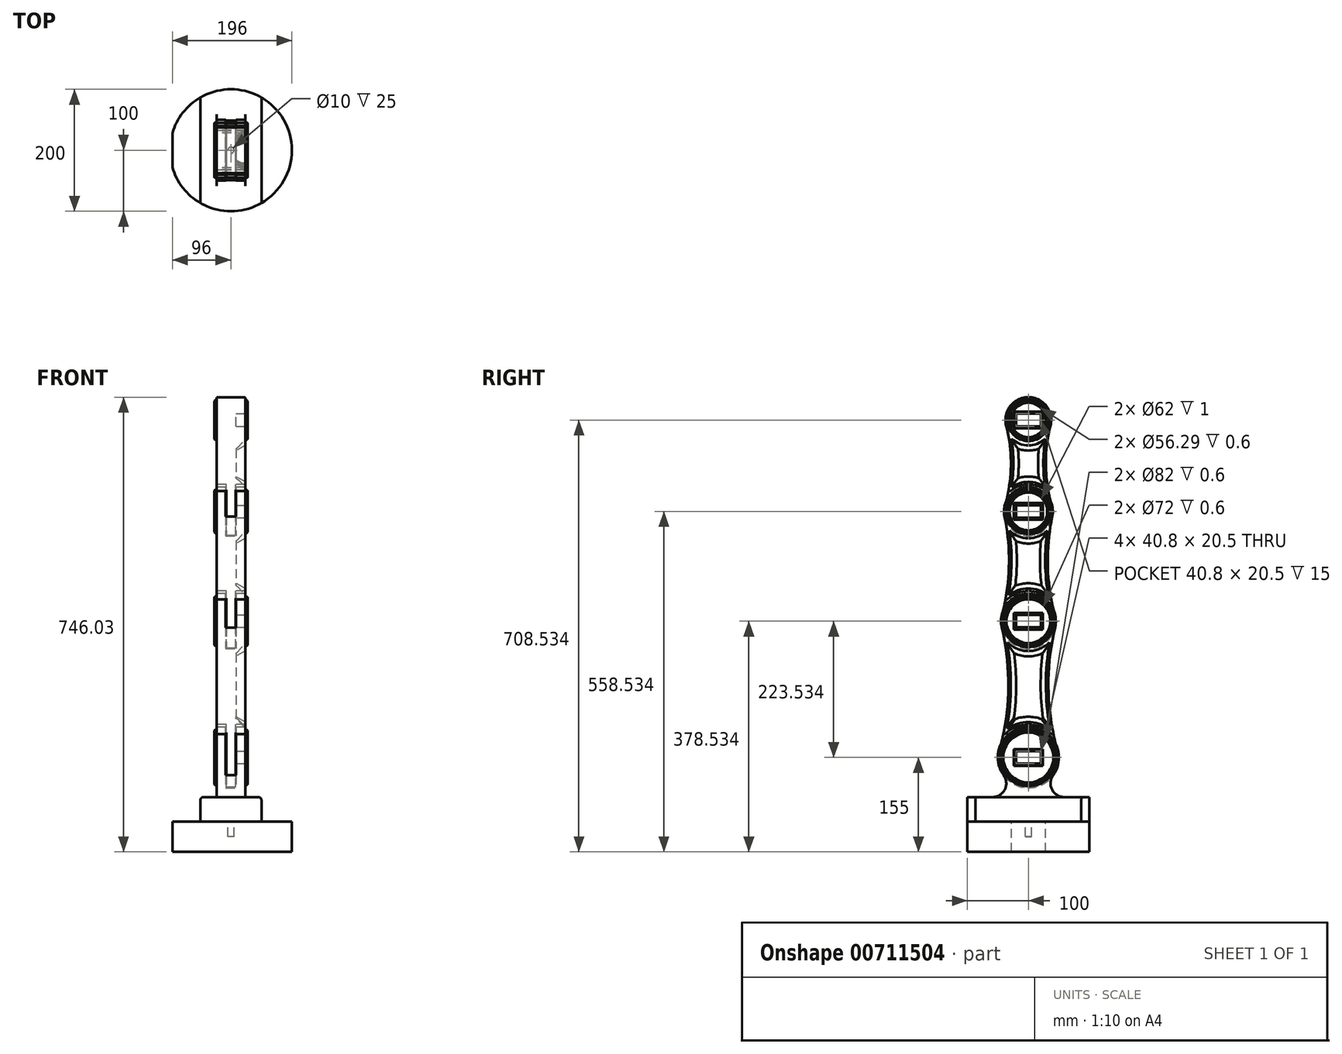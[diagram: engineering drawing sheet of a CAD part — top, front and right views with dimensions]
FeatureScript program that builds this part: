
annotation { "Feature Type Name" : "Feature", "Feature Type Description" : "" }
export const myFeature = defineFeature(function(context is Context, id is Id, definition is map)
    precondition{}
    {
        {
            var Q0;
            Q0=qCreatedBy(makeId("Top.planeOp"),FACE);
            var sketch = newSketch(context, id + "F0", { "sketchPlane" : qUnion([Q0])});
            skArc(sketch, "E0", {"start": v(-96, -28) * mm, "mid": v(100, 0) * mm, "end": v(-96, 28) * mm});
            skLineSegment(sketch, "E1", {"start": v(-50, 86.6) * mm, "end": v(-50, -86.6) * mm});
            skLineSegment(sketch, "E2", {"start": v(50, 86.6) * mm, "end": v(50, -86.6) * mm});
            skLineSegment(sketch, "E3", {"start": v(-96, 28) * mm, "end": v(-96, -28) * mm});
            skSolve(sketch);
        }
        {
            var Q0;
            Q0 = qSketchRegion(id + "F0", true);
            extrude(context, id + "F1", {"entities" : qUnion([Q0]), "oppositeDirection" : true, "depth" : 50 * mm, "offsetDistance" : 25 * mm});
        }
        {
            var Q0;
            {var subQ0=sQuery(id+"F0.wireOp",EDGE,"E1");Q0=makeQuery(id+"F0.imprint","IMPRINT",FACE,{"disambiguationData":[TD([[makeQuery(id+"F0.imprint","IMPRINT",EDGE,{"derivedFrom":subQ0}),1.0]])]});}
            extrude(context, id + "F2", {"entities" : qUnion([Q0]), "depth" : 40 * mm, "offsetDistance" : 25 * mm});
        }
        {
            var Q0;
            Q0=qCreatedBy(makeId("Right.planeOp"),FACE);
            var sketch = newSketch(context, id + "F3", { "sketchPlane" : qUnion([Q0])});
            skCircle(sketch, "E4", {"center": v(0, 105) * mm, "radius": 50 * mm});
            skArc(sketch, "E5", {"start": v(-58.74, 40) * mm, "mid": v(-38.7, 52.27) * mm, "end": v(-40.5, 75.69) * mm});
            skArc(sketch, "E6", {"start": v(40.5, 75.69) * mm, "mid": v(38.7, 52.27) * mm, "end": v(58.74, 40) * mm});
            skLineSegment(sketch, "E7", {"start": v(-58.74, 40) * mm, "end": v(58.74, 40) * mm});
            skSolve(sketch);
        }
        {
            var Q0;
            Q0 = qSketchRegion(id + "F3", true);
            extrude(context, id + "F4", {"entities" : qUnion([Q0]), "operationType" : NewBodyOperationType.ADD, "endBound" : BoundingType.SYMMETRIC, "depth" : 47 * mm, "offsetDistance" : 25 * mm});
        }
        {
            var Q0;
            {var subQ0=sQuery(id+"F3.wireOp",EDGE,"E4");var subQ1=makeQuery(id+"F3.imprint","INTERSECT",VERTEX,{"derivedFrom":[subQ0,sQuery(id+"F3.wireOp",EDGE,"E5")]});Q0=makeQuery(id+"F3.imprint","IMPRINT",FACE,{"disambiguationData":[TD([[makeQuery(id+"F3.imprint","IMPRINT",EDGE,{"disambiguationData":[TD([[subQ1,-1.0]])],"derivedFrom":subQ0}),1.0]])]});}
            extrude(context, id + "F5", {"entities" : qUnion([Q0]), "operationType" : NewBodyOperationType.REMOVE, "endBound" : BoundingType.SYMMETRIC, "oppositeDirection" : true, "depth" : 17 * mm, "offsetDistance" : 25 * mm});
        }
        {
            var Q0;
            Q0=qCreatedBy(makeId("Right.planeOp"),FACE);
            var sketch = newSketch(context, id + "F6", { "sketchPlane" : qUnion([Q0])});
            skCircle(sketch, "E8.0", {"center": v(0, 105) * mm, "radius": 49 * mm});
            skCircle(sketch, "E9", {"center": v(0, 328.53) * mm, "radius": 45 * mm});
            skArc(sketch, "E10", {"start": v(-47.22, 118.07) * mm, "mid": v(-32.8, 217.84) * mm, "end": v(-43.76, 318.04) * mm});
            skArc(sketch, "E11", {"start": v(43.76, 318.04) * mm, "mid": v(32.8, 217.84) * mm, "end": v(47.22, 118.07) * mm});
            skArc(sketch, "E12.0", {"start": v(42.07, 138.86) * mm, "mid": v(0, 159) * mm, "end": v(-42.07, 138.86) * mm});
            skArc(sketch, "E13.0", {"start": v(-34.7, 293.93) * mm, "mid": v(0, 279.53) * mm, "end": v(34.7, 293.93) * mm});
            skArc(sketch, "E14.0", {"start": v(34.7, 293.93) * mm, "mid": v(28.74, 222.34) * mm, "end": v(35.56, 150.82) * mm});
            skArc(sketch, "E15.0", {"start": v(-35.56, 150.82) * mm, "mid": v(-28.74, 222.34) * mm, "end": v(-34.7, 293.93) * mm});
            skArc(sketch, "E16.0", {"start": v(35.56, 150.82) * mm, "mid": v(0, 163) * mm, "end": v(-35.56, 150.82) * mm});
            skSolve(sketch);
        }
        {
            var Q0;
            Q0 = qSketchRegion(id + "F6", true);
            extrude(context, id + "F7", {"entities" : qUnion([Q0]), "endBound" : BoundingType.SYMMETRIC, "depth" : 15 * mm, "offsetDistance" : 25 * mm});
        }
        {
            var Q0;
            {var subQ5=sQuery(id+"F6.wireOp",EDGE,"E12.0");Q0=makeQuery(id+"F6.imprint","IMPRINT",FACE,{"disambiguationData":[TD([[makeQuery(id+"F6.imprint","IMPRINT",EDGE,{"derivedFrom":subQ5}),-1.0]])]});}
            var Q1;
            {var subQ0=sQuery(id+"F6.wireOp",EDGE,"E9");var subQ1=makeQuery(id+"F6.imprint","INTERSECT",VERTEX,{"derivedFrom":[subQ0,sQuery(id+"F6.wireOp",EDGE,"E10")]});Q1=makeQuery(id+"F6.imprint","IMPRINT",FACE,{"disambiguationData":[TD([[makeQuery(id+"F6.imprint","IMPRINT",EDGE,{"disambiguationData":[TD([[subQ1,-1.0]])],"derivedFrom":subQ0}),1.0]])]});}
            var Q2;
            Q2=makeQuery(id+"F6.imprint","IMPRINT",FACE,{"disambiguationData":[TD([[makeQuery(id+"F6.imprint","IMPRINT",EDGE,{"derivedFrom":sQuery(id+"F6.wireOp",EDGE,"E13.0")}),-1.0]])]});
            extrude(context, id + "F8", {"entities" : qUnion([Q0, Q1, Q2]), "operationType" : NewBodyOperationType.ADD, "endBound" : BoundingType.SYMMETRIC, "depth" : 47 * mm, "offsetDistance" : 25 * mm});
        }
        {
            var Q0;
            Q0=makeQuery(id+"F8.opExtrude","CAP_FACE",FACE,{"disambiguationData":[OSD([sQuery(id+"F6.wireOp",EDGE,"E9"),sQuery(id+"F6.wireOp",EDGE,"E10"),sQuery(id+"F6.wireOp",EDGE,"E11"),sQuery(id+"F6.wireOp",EDGE,"E12.0")])],"isStart":false});
            var sketch = newSketch(context, id + "F9", { "sketchPlane" : qUnion([Q0])});
            skArc(sketch, "E17.0", {"start": v(-35.56, 150.82) * mm, "mid": v(0, 163) * mm, "end": v(35.56, 150.82) * mm});
            skArc(sketch, "E17.1", {"start": v(-34.7, 293.93) * mm, "mid": v(-28.74, 222.34) * mm, "end": v(-35.56, 150.82) * mm});
            skArc(sketch, "E17.2", {"start": v(34.7, 293.93) * mm, "mid": v(0, 279.53) * mm, "end": v(-34.7, 293.93) * mm});
            skArc(sketch, "E17.3", {"start": v(35.56, 150.82) * mm, "mid": v(28.74, 222.34) * mm, "end": v(34.7, 293.93) * mm});
            skSolve(sketch);
        }
        {
            var Q0;
            Q0 = qSketchRegion(id + "F9", true);
            extrude(context, id + "F10", {"entities" : qUnion([Q0]), "operationType" : NewBodyOperationType.REMOVE, "oppositeDirection" : true, "depth" : 15 * mm, "offsetDistance" : 25 * mm, "hasDraft" : true, "draftAngle" : 30 * degree, "draftPullDirection" : true});
        }
        {
            var Q0;
            {var subQ0=sQuery(id+"F6.wireOp",EDGE,"E9");var subQ1=makeQuery(id+"F6.imprint","INTERSECT",VERTEX,{"derivedFrom":[subQ0,sQuery(id+"F6.wireOp",EDGE,"E10")]});Q0=makeQuery(id+"F6.imprint","IMPRINT",FACE,{"disambiguationData":[TD([[makeQuery(id+"F6.imprint","IMPRINT",EDGE,{"disambiguationData":[TD([[subQ1,-1.0]])],"derivedFrom":subQ0}),1.0]])]});}
            extrude(context, id + "F11", {"entities" : qUnion([Q0]), "operationType" : NewBodyOperationType.REMOVE, "endBound" : BoundingType.SYMMETRIC, "oppositeDirection" : true, "depth" : 17 * mm, "offsetDistance" : 25 * mm});
        }
        {
            var Q0;
            Q0=qCreatedBy(makeId("Right.planeOp"),FACE);
            var sketch = newSketch(context, id + "F12", { "sketchPlane" : qUnion([Q0])});
            skCircle(sketch, "E18", {"center": v(0, 328.53) * mm, "radius": 44.5 * mm});
            skCircle(sketch, "E19", {"center": v(0, 508.53) * mm, "radius": 40 * mm});
            skArc(sketch, "E20", {"start": v(-43.05, 339.8) * mm, "mid": v(-31.77, 419.82) * mm, "end": v(-39.15, 500.3) * mm});
            skArc(sketch, "E21", {"start": v(39.15, 500.3) * mm, "mid": v(31.77, 419.82) * mm, "end": v(43.05, 339.8) * mm});
            skArc(sketch, "E22.0", {"start": v(38.46, 359.69) * mm, "mid": v(0, 378.03) * mm, "end": v(-38.46, 359.69) * mm});
            skSolve(sketch);
        }
        {
            var Q0;
            Q0 = qSketchRegion(id + "F12", true);
            extrude(context, id + "F13", {"entities" : qUnion([Q0]), "endBound" : BoundingType.SYMMETRIC, "depth" : 15 * mm, "offsetDistance" : 25 * mm});
        }
        {
            var Q0;
            {var subQ0=sQuery(id+"F12.wireOp",EDGE,"E19");var subQ1=makeQuery(id+"F12.imprint","INTERSECT",VERTEX,{"derivedFrom":[subQ0,sQuery(id+"F12.wireOp",EDGE,"E20")]});Q0=makeQuery(id+"F12.imprint","IMPRINT",FACE,{"disambiguationData":[TD([[makeQuery(id+"F12.imprint","IMPRINT",EDGE,{"disambiguationData":[TD([[subQ1,-1.0]])],"derivedFrom":subQ0}),1.0]])]});}
            var Q1;
            {var subQ5=sQuery(id+"F12.wireOp",EDGE,"E22.0");Q1=makeQuery(id+"F12.imprint","IMPRINT",FACE,{"disambiguationData":[TD([[makeQuery(id+"F12.imprint","IMPRINT",EDGE,{"derivedFrom":subQ5}),-1.0]])]});}
            extrude(context, id + "F14", {"entities" : qUnion([Q0, Q1]), "operationType" : NewBodyOperationType.ADD, "endBound" : BoundingType.SYMMETRIC, "depth" : 47 * mm, "offsetDistance" : 25 * mm});
        }
        {
            var Q0;
            Q0=makeQuery(id+"F14.opExtrude","CAP_FACE",FACE,{"disambiguationData":[OSD([sQuery(id+"F12.wireOp",EDGE,"E19"),sQuery(id+"F12.wireOp",EDGE,"E20"),sQuery(id+"F12.wireOp",EDGE,"E21"),sQuery(id+"F12.wireOp",EDGE,"E22.0")])],"isStart":false});
            var sketch = newSketch(context, id + "F15", { "sketchPlane" : qUnion([Q0])});
            skArc(sketch, "E23.0", {"start": v(-32.31, 371.17) * mm, "mid": v(0, 382.03) * mm, "end": v(32.31, 371.17) * mm});
            skArc(sketch, "E23.1", {"start": v(-31.08, 477.39) * mm, "mid": v(-27.69, 424.23) * mm, "end": v(-32.31, 371.17) * mm});
            skArc(sketch, "E23.2", {"start": v(31.08, 477.39) * mm, "mid": v(0, 464.53) * mm, "end": v(-31.08, 477.39) * mm});
            skArc(sketch, "E23.3", {"start": v(32.31, 371.17) * mm, "mid": v(27.69, 424.23) * mm, "end": v(31.08, 477.39) * mm});
            skSolve(sketch);
        }
        {
            var Q0;
            Q0 = qSketchRegion(id + "F15", true);
            extrude(context, id + "F16", {"entities" : qUnion([Q0]), "operationType" : NewBodyOperationType.REMOVE, "oppositeDirection" : true, "depth" : 15 * mm, "offsetDistance" : 25 * mm, "hasDraft" : true, "draftAngle" : 30 * degree, "draftPullDirection" : true});
        }
        {
            var Q0;
            {var subQ0=sQuery(id+"F12.wireOp",EDGE,"E19");var subQ1=makeQuery(id+"F12.imprint","INTERSECT",VERTEX,{"derivedFrom":[subQ0,sQuery(id+"F12.wireOp",EDGE,"E20")]});Q0=makeQuery(id+"F12.imprint","IMPRINT",FACE,{"disambiguationData":[TD([[makeQuery(id+"F12.imprint","IMPRINT",EDGE,{"disambiguationData":[TD([[subQ1,-1.0]])],"derivedFrom":subQ0}),1.0]])]});}
            extrude(context, id + "F17", {"entities" : qUnion([Q0]), "operationType" : NewBodyOperationType.REMOVE, "endBound" : BoundingType.SYMMETRIC, "oppositeDirection" : true, "depth" : 17 * mm, "offsetDistance" : 25 * mm});
        }
        {
            var Q0;
            Q0=qCreatedBy(makeId("Right.planeOp"),FACE);
            var sketch = newSketch(context, id + "F18", { "sketchPlane" : qUnion([Q0])});
            skCircle(sketch, "E24", {"center": v(0, 508.53) * mm, "radius": 39.5 * mm});
            skCircle(sketch, "E25", {"center": v(0, 658.53) * mm, "radius": 37.5 * mm});
            skArc(sketch, "E26", {"start": v(-38, 519.3) * mm, "mid": v(-28.58, 584.16) * mm, "end": v(-36.33, 649.25) * mm});
            skArc(sketch, "E27", {"start": v(36.33, 649.25) * mm, "mid": v(28.58, 584.16) * mm, "end": v(38, 519.3) * mm});
            skArc(sketch, "E28.0", {"start": v(33.52, 537.8) * mm, "mid": v(0, 553.03) * mm, "end": v(-33.52, 537.8) * mm});
            skSolve(sketch);
        }
        {
            var Q0;
            Q0 = qSketchRegion(id + "F18", true);
            extrude(context, id + "F19", {"entities" : qUnion([Q0]), "endBound" : BoundingType.SYMMETRIC, "depth" : 15 * mm, "offsetDistance" : 25 * mm});
        }
        {
            var Q0;
            {var subQ5=sQuery(id+"F18.wireOp",EDGE,"E28.0");Q0=makeQuery(id+"F18.imprint","IMPRINT",FACE,{"disambiguationData":[TD([[makeQuery(id+"F18.imprint","IMPRINT",EDGE,{"derivedFrom":subQ5}),-1.0]])]});}
            var Q1;
            {var subQ0=sQuery(id+"F18.wireOp",EDGE,"E25");var subQ1=makeQuery(id+"F18.imprint","INTERSECT",VERTEX,{"derivedFrom":[subQ0,sQuery(id+"F18.wireOp",EDGE,"E26")]});Q1=makeQuery(id+"F18.imprint","IMPRINT",FACE,{"disambiguationData":[TD([[makeQuery(id+"F18.imprint","IMPRINT",EDGE,{"disambiguationData":[TD([[subQ1,-1.0]])],"derivedFrom":subQ0}),1.0]])]});}
            extrude(context, id + "F20", {"entities" : qUnion([Q0, Q1]), "operationType" : NewBodyOperationType.ADD, "endBound" : BoundingType.SYMMETRIC, "depth" : 47 * mm, "offsetDistance" : 25 * mm});
        }
        {
            var Q0;
            Q0=makeQuery(id+"F20.opExtrude","CAP_FACE",FACE,{"disambiguationData":[OSD([sQuery(id+"F18.wireOp",EDGE,"E25"),sQuery(id+"F18.wireOp",EDGE,"E26"),sQuery(id+"F18.wireOp",EDGE,"E27"),sQuery(id+"F18.wireOp",EDGE,"E28.0")])],"isStart":false});
            var sketch = newSketch(context, id + "F21", { "sketchPlane" : qUnion([Q0])});
            skArc(sketch, "E29.0", {"start": v(-27.56, 548.44) * mm, "mid": v(0, 557.03) * mm, "end": v(27.56, 548.44) * mm});
            skArc(sketch, "E29.1", {"start": v(-27.78, 627.7) * mm, "mid": v(-24.56, 588.08) * mm, "end": v(-27.56, 548.44) * mm});
            skArc(sketch, "E29.2", {"start": v(27.78, 627.7) * mm, "mid": v(0, 617.03) * mm, "end": v(-27.78, 627.7) * mm});
            skArc(sketch, "E29.3", {"start": v(27.56, 548.44) * mm, "mid": v(24.56, 588.08) * mm, "end": v(27.78, 627.7) * mm});
            skSolve(sketch);
        }
        {
            var Q0;
            Q0 = qSketchRegion(id + "F21", true);
            extrude(context, id + "F22", {"entities" : qUnion([Q0]), "operationType" : NewBodyOperationType.REMOVE, "oppositeDirection" : true, "depth" : 15 * mm, "offsetDistance" : 25 * mm, "hasDraft" : true, "draftAngle" : 30 * degree, "draftPullDirection" : true});
        }
        {
            var Q0;
            Q0=qCreatedBy(makeId("Front.planeOp"),FACE);
            var sketch = newSketch(context, id + "F23", { "sketchPlane" : qUnion([Q0])});
            skLineSegment(sketch, "E30", {"start": v(27.5, 149) * mm, "end": v(27.5, 146) * mm});
            skLineSegment(sketch, "E31", {"start": v(27.5, 149) * mm, "end": v(23.5, 152.36) * mm});
            skLineSegment(sketch, "E32", {"start": v(23.5, 152.36) * mm, "end": v(23.5, 105) * mm});
            skLineSegment(sketch, "E33", {"start": v(23.5, 105) * mm, "end": v(26.9, 105) * mm});
            skLineSegment(sketch, "E34.MirrorCS", {"start": v(-23.5, 152.36) * mm, "end": v(-23.5, 105) * mm});
            skLineSegment(sketch, "E35.MirrorCS", {"start": v(-23.5, 105) * mm, "end": v(-26.9, 105) * mm});
            skLineSegment(sketch, "E36.MirrorCS", {"start": v(-27.5, 149) * mm, "end": v(-27.5, 146) * mm});
            skLineSegment(sketch, "E37.MirrorCS", {"start": v(-27.5, 149) * mm, "end": v(-23.5, 152.36) * mm});
            skLineSegment(sketch, "E38", {"start": v(27.5, 367.53) * mm, "end": v(27.5, 364.53) * mm});
            skLineSegment(sketch, "E39", {"start": v(27.5, 367.53) * mm, "end": v(23.5, 370.89) * mm});
            skLineSegment(sketch, "E40", {"start": v(26.9, 328.53) * mm, "end": v(23.5, 328.53) * mm});
            skLineSegment(sketch, "E41", {"start": v(23.5, 328.53) * mm, "end": v(23.5, 370.89) * mm});
            skLineSegment(sketch, "E42.MirrorCS", {"start": v(-27.5, 367.53) * mm, "end": v(-27.5, 364.53) * mm});
            skLineSegment(sketch, "E43.MirrorCS", {"start": v(-27.5, 367.53) * mm, "end": v(-23.5, 370.89) * mm});
            skLineSegment(sketch, "E44.MirrorCS", {"start": v(-23.5, 328.53) * mm, "end": v(-23.5, 370.89) * mm});
            skLineSegment(sketch, "E45.MirrorCS", {"start": v(-26.9, 328.53) * mm, "end": v(-23.5, 328.53) * mm});
            skLineSegment(sketch, "E46", {"start": v(27.5, 542.53) * mm, "end": v(27.5, 539.53) * mm});
            skLineSegment(sketch, "E47", {"start": v(27.5, 542.53) * mm, "end": v(23.5, 545.89) * mm});
            skLineSegment(sketch, "E48", {"start": v(26.5, 508.53) * mm, "end": v(23.5, 508.53) * mm});
            skLineSegment(sketch, "E49", {"start": v(23.5, 508.53) * mm, "end": v(23.5, 545.89) * mm});
            skLineSegment(sketch, "E50.MirrorCS", {"start": v(-27.5, 542.53) * mm, "end": v(-27.5, 539.53) * mm});
            skLineSegment(sketch, "E51.MirrorCS", {"start": v(-23.5, 508.53) * mm, "end": v(-23.5, 545.89) * mm});
            skLineSegment(sketch, "E52.MirrorCS", {"start": v(-26.5, 508.53) * mm, "end": v(-23.5, 508.53) * mm});
            skLineSegment(sketch, "E53.MirrorCS", {"start": v(-27.5, 542.53) * mm, "end": v(-23.5, 545.89) * mm});
            skLineSegment(sketch, "E54", {"start": v(27.5, 689.68) * mm, "end": v(27.5, 686.68) * mm});
            skLineSegment(sketch, "E55", {"start": v(26.9, 658.53) * mm, "end": v(23.5, 658.53) * mm});
            skLineSegment(sketch, "E56", {"start": v(23.5, 658.53) * mm, "end": v(23.5, 693.03) * mm});
            skLineSegment(sketch, "E57", {"start": v(23.5, 693.03) * mm, "end": v(27.5, 689.68) * mm});
            skLineSegment(sketch, "E58.MirrorCS", {"start": v(-27.5, 689.68) * mm, "end": v(-27.5, 686.68) * mm});
            skLineSegment(sketch, "E59.MirrorCS", {"start": v(-23.5, 658.53) * mm, "end": v(-23.5, 693.03) * mm});
            skLineSegment(sketch, "E60.MirrorCS", {"start": v(-26.9, 658.53) * mm, "end": v(-23.5, 658.53) * mm});
            skLineSegment(sketch, "E61.MirrorCS", {"start": v(-23.5, 693.03) * mm, "end": v(-27.5, 689.68) * mm});
            skLineSegment(sketch, "E62.top", {"start": v(27.5, 146) * mm, "end": v(26.9, 146) * mm});
            skLineSegment(sketch, "E62.right", {"start": v(26.9, 105) * mm, "end": v(26.9, 146) * mm});
            skPoint(sketch, "E62.bottom.start.orphan", {"position": v(27.5, 105) * mm});
            skLineSegment(sketch, "E63.MirrorCS", {"start": v(-26.9, 105) * mm, "end": v(-26.9, 146) * mm});
            skLineSegment(sketch, "E64.MirrorCS", {"start": v(-27.5, 146) * mm, "end": v(-26.9, 146) * mm});
            skPoint(sketch, "E65.orphan", {"position": v(-27.5, 105) * mm});
            skLineSegment(sketch, "E66", {"start": v(27.5, 364.53) * mm, "end": v(26.9, 364.53) * mm});
            skLineSegment(sketch, "E67", {"start": v(26.9, 364.53) * mm, "end": v(26.9, 328.53) * mm});
            skPoint(sketch, "E68.orphan", {"position": v(27.5, 328.53) * mm});
            skLineSegment(sketch, "E69.MirrorCS", {"start": v(-26.9, 364.53) * mm, "end": v(-26.9, 328.53) * mm});
            skLineSegment(sketch, "E70.MirrorCS", {"start": v(-27.5, 364.53) * mm, "end": v(-26.9, 364.53) * mm});
            skPoint(sketch, "E71.orphan", {"position": v(-27.5, 328.53) * mm});
            skLineSegment(sketch, "E72", {"start": v(27.5, 539.53) * mm, "end": v(26.5, 539.53) * mm});
            skLineSegment(sketch, "E73", {"start": v(26.5, 539.53) * mm, "end": v(26.5, 508.53) * mm});
            skPoint(sketch, "E74.orphan", {"position": v(27.5, 508.53) * mm});
            skLineSegment(sketch, "E75.MirrorCS", {"start": v(-26.5, 539.53) * mm, "end": v(-26.5, 508.53) * mm});
            skLineSegment(sketch, "E76.MirrorCS", {"start": v(-27.5, 539.53) * mm, "end": v(-26.5, 539.53) * mm});
            skPoint(sketch, "E77.orphan", {"position": v(-27.5, 508.53) * mm});
            skLineSegment(sketch, "E78", {"start": v(27.5, 686.68) * mm, "end": v(26.9, 686.68) * mm});
            skLineSegment(sketch, "E79", {"start": v(26.9, 686.68) * mm, "end": v(26.9, 658.53) * mm});
            skPoint(sketch, "E80.orphan", {"position": v(27.5, 658.53) * mm});
            skLineSegment(sketch, "E81.MirrorCS", {"start": v(-26.9, 686.68) * mm, "end": v(-26.9, 658.53) * mm});
            skLineSegment(sketch, "E82.MirrorCS", {"start": v(-27.5, 686.68) * mm, "end": v(-26.9, 686.68) * mm});
            skPoint(sketch, "E83.orphan", {"position": v(-27.5, 658.53) * mm});
            skSolve(sketch);
        }
        {
            var Q0;
            Q0=makeQuery(id+"F23.imprint","IMPRINT",FACE,{"disambiguationData":[TD([[makeQuery(id+"F23.imprint","IMPRINT",EDGE,{"derivedFrom":sQuery(id+"F23.wireOp",EDGE,"E30")}),-1.0]])]});
            var Q1;
            Q1=makeQuery(id+"F23.imprint","IMPRINT",FACE,{"disambiguationData":[TD([[makeQuery(id+"F23.imprint","IMPRINT",EDGE,{"derivedFrom":sQuery(id+"F23.wireOp",EDGE,"E34.MirrorCS")}),-1.0]])]});
            var Q2;
            Q2=sQuery(id+"F23.wireOp",EDGE,"E35.MirrorCS");
            revolve(context, id + "F24", {"surfaceOperationType" : NewSurfaceOperationType.NEW, "entities" : qUnion([Q0, Q1]), "axis" : qUnion([Q2]), "revolveType" : RevolveType.FULL});
        }
        {
            var Q0;
            Q0=makeQuery(id+"F23.imprint","IMPRINT",FACE,{"disambiguationData":[TD([[makeQuery(id+"F23.imprint","IMPRINT",EDGE,{"derivedFrom":sQuery(id+"F23.wireOp",EDGE,"E38")}),-1.0]])]});
            var Q1;
            Q1=makeQuery(id+"F23.imprint","IMPRINT",FACE,{"disambiguationData":[TD([[makeQuery(id+"F23.imprint","IMPRINT",EDGE,{"derivedFrom":sQuery(id+"F23.wireOp",EDGE,"E42.MirrorCS")}),1.0]])]});
            var Q2;
            Q2=sQuery(id+"F23.wireOp",EDGE,"E45.MirrorCS");
            revolve(context, id + "F25", {"surfaceOperationType" : NewSurfaceOperationType.NEW, "entities" : qUnion([Q0, Q1]), "axis" : qUnion([Q2]), "revolveType" : RevolveType.FULL});
        }
        {
            var Q0;
            Q0=makeQuery(id+"F23.imprint","IMPRINT",FACE,{"disambiguationData":[TD([[makeQuery(id+"F23.imprint","IMPRINT",EDGE,{"derivedFrom":sQuery(id+"F23.wireOp",EDGE,"E50.MirrorCS")}),1.0]])]});
            var Q1;
            Q1=makeQuery(id+"F23.imprint","IMPRINT",FACE,{"disambiguationData":[TD([[makeQuery(id+"F23.imprint","IMPRINT",EDGE,{"derivedFrom":sQuery(id+"F23.wireOp",EDGE,"E46")}),-1.0]])]});
            var Q2;
            Q2=sQuery(id+"F23.wireOp",EDGE,"E52.MirrorCS");
            revolve(context, id + "F26", {"surfaceOperationType" : NewSurfaceOperationType.NEW, "entities" : qUnion([Q0, Q1]), "axis" : qUnion([Q2]), "revolveType" : RevolveType.FULL});
        }
        {
            var Q0;
            Q0=makeQuery(id+"F23.imprint","IMPRINT",FACE,{"disambiguationData":[TD([[makeQuery(id+"F23.imprint","IMPRINT",EDGE,{"derivedFrom":sQuery(id+"F23.wireOp",EDGE,"E54")}),-1.0]])]});
            var Q1;
            Q1=makeQuery(id+"F23.imprint","IMPRINT",FACE,{"disambiguationData":[TD([[makeQuery(id+"F23.imprint","IMPRINT",EDGE,{"derivedFrom":sQuery(id+"F23.wireOp",EDGE,"E58.MirrorCS")}),1.0]])]});
            var Q2;
            Q2=sQuery(id+"F23.wireOp",EDGE,"E55");
            revolve(context, id + "F27", {"surfaceOperationType" : NewSurfaceOperationType.NEW, "entities" : qUnion([Q0, Q1]), "axis" : qUnion([Q2]), "revolveType" : RevolveType.FULL});
        }
        {
            var Q0;
            Q0=makeQuery(id+"F4.opExtrude","CAP_FACE",FACE,{"disambiguationData":[OSD([sQuery(id+"F3.wireOp",EDGE,"E4"),sQuery(id+"F3.wireOp",EDGE,"E5"),sQuery(id+"F3.wireOp",EDGE,"E6"),sQuery(id+"F3.wireOp",EDGE,"E7")])],"isStart":false});
            var sketch = newSketch(context, id + "F28", { "sketchPlane" : qUnion([Q0])});
            skLineSegment(sketch, "E84.bottom", {"start": v(-20.4, 115.25) * mm, "end": v(20.4, 115.25) * mm});
            skLineSegment(sketch, "E84.top", {"start": v(-20.4, 94.75) * mm, "end": v(20.4, 94.75) * mm});
            skLineSegment(sketch, "E84.left", {"start": v(-20.4, 115.25) * mm, "end": v(-20.4, 94.75) * mm});
            skLineSegment(sketch, "E84.right", {"start": v(20.4, 115.25) * mm, "end": v(20.4, 94.75) * mm});
            skCircle(sketch, "E85", {"center": v(0, 105) * mm, "radius": 50 * mm});
            skLineSegment(sketch, "E86", {"start": v(0, 115.25) * mm, "end": v(0, 94.75) * mm, "construction": true});
            skLineSegment(sketch, "E87", {"start": v(-20.4, 105) * mm, "end": v(20.4, 105) * mm, "construction": true});
            skCircle(sketch, "E88", {"center": v(0, 328.53) * mm, "radius": 45 * mm});
            skLineSegment(sketch, "E89.bottom", {"start": v(-20.4, 318.28) * mm, "end": v(20.4, 318.28) * mm});
            skLineSegment(sketch, "E89.top", {"start": v(-20.4, 338.78) * mm, "end": v(20.4, 338.78) * mm});
            skLineSegment(sketch, "E89.left", {"start": v(-20.4, 318.28) * mm, "end": v(-20.4, 338.78) * mm});
            skLineSegment(sketch, "E89.right", {"start": v(20.4, 318.28) * mm, "end": v(20.4, 338.78) * mm});
            skLineSegment(sketch, "E90", {"start": v(0, 338.78) * mm, "end": v(0, 318.28) * mm, "construction": true});
            skCircle(sketch, "E91", {"center": v(0, 508.53) * mm, "radius": 40 * mm});
            skLineSegment(sketch, "E92.bottom", {"start": v(-20.4, 498.28) * mm, "end": v(20.4, 498.28) * mm});
            skLineSegment(sketch, "E92.top", {"start": v(-20.4, 518.78) * mm, "end": v(20.4, 518.78) * mm});
            skLineSegment(sketch, "E92.left", {"start": v(-20.4, 498.28) * mm, "end": v(-20.4, 518.78) * mm});
            skLineSegment(sketch, "E92.right", {"start": v(20.4, 498.28) * mm, "end": v(20.4, 518.78) * mm});
            skLineSegment(sketch, "E93", {"start": v(0, 518.78) * mm, "end": v(0, 498.28) * mm, "construction": true});
            skCircle(sketch, "E94", {"center": v(0, 658.53) * mm, "radius": 37.5 * mm});
            skLineSegment(sketch, "E95.bottom", {"start": v(-20.4, 648.28) * mm, "end": v(20.4, 648.28) * mm});
            skLineSegment(sketch, "E95.top", {"start": v(-20.4, 668.78) * mm, "end": v(20.4, 668.78) * mm});
            skLineSegment(sketch, "E95.left", {"start": v(-20.4, 648.28) * mm, "end": v(-20.4, 668.78) * mm});
            skLineSegment(sketch, "E95.right", {"start": v(20.4, 648.28) * mm, "end": v(20.4, 668.78) * mm});
            skLineSegment(sketch, "E96", {"start": v(0, 668.78) * mm, "end": v(0, 648.28) * mm, "construction": true});
            skSolve(sketch);
        }
        {
            var Q0;
            Q0=makeQuery(id+"F28.imprint","IMPRINT",FACE,{"disambiguationData":[TD([[makeQuery(id+"F28.imprint","IMPRINT",EDGE,{"derivedFrom":sQuery(id+"F28.wireOp",EDGE,"E84.bottom")}),-1.0]])]});
            var Q1;
            Q1=makeQuery(id+"F28.imprint","IMPRINT",FACE,{"disambiguationData":[TD([[makeQuery(id+"F28.imprint","IMPRINT",EDGE,{"derivedFrom":sQuery(id+"F28.wireOp",EDGE,"E89.bottom")}),1.0]])]});
            var Q2;
            Q2=makeQuery(id+"F28.imprint","IMPRINT",FACE,{"disambiguationData":[TD([[makeQuery(id+"F28.imprint","IMPRINT",EDGE,{"derivedFrom":sQuery(id+"F28.wireOp",EDGE,"E92.bottom")}),1.0]])]});
            var Q3;
            Q3=makeQuery(id+"F28.imprint","IMPRINT",FACE,{"disambiguationData":[TD([[makeQuery(id+"F28.imprint","IMPRINT",EDGE,{"derivedFrom":sQuery(id+"F28.wireOp",EDGE,"E95.bottom")}),1.0]])]});
            extrude(context, id + "F29", {"entities" : qUnion([Q0, Q1, Q2, Q3]), "operationType" : NewBodyOperationType.REMOVE, "endBound" : BoundingType.SYMMETRIC, "oppositeDirection" : true, "depth" : 30 * mm, "offsetDistance" : 25 * mm});
        }
        {
            var Q0;
            Q0=makeQuery(id+"F1.opExtrude","CAP_FACE",FACE,{"disambiguationData":[OSD([sQuery(id+"F0.wireOp",EDGE,"E0"),sQuery(id+"F0.wireOp",EDGE,"E3")])],"isStart":true});
            var sketch = newSketch(context, id + "F30", { "sketchPlane" : qUnion([Q0])});
            skCircle(sketch, "E97", {"center": v(0, 0) * mm, "radius": 100 * mm});
            skCircle(sketch, "E98", {"center": v(0, 0) * mm, "radius": 5 * mm});
            skSolve(sketch);
        }
        {
            var Q0;
            Q0=makeQuery(id+"F30.imprint","IMPRINT",FACE,{"disambiguationData":[TD([[makeQuery(id+"F30.imprint","IMPRINT",EDGE,{"derivedFrom":sQuery(id+"F30.wireOp",EDGE,"E98")}),1.0]])]});
            extrude(context, id + "F31", {"entities" : qUnion([Q0]), "operationType" : NewBodyOperationType.REMOVE, "oppositeDirection" : true, "depth" : 25 * mm, "offsetDistance" : 25 * mm});
        }
        {
            var Q0;
            Q0=makeQuery(id+"F2.opExtrude","CAP_EDGE",EDGE,{"disambiguationData":[OSD([sQuery(id+"F0.wireOp",EDGE,"E1")])],"isStart":false});
            var Q1;
            Q1=makeQuery(id+"F2.opExtrude","CAP_EDGE",EDGE,{"disambiguationData":[OSD([sQuery(id+"F0.wireOp",EDGE,"E2")])],"isStart":false});
            var Q2;
            Q2=makeQuery(id+"F4.opExtrude","CAP_EDGE",EDGE,{"disambiguationData":[OSD([sQuery(id+"F3.wireOp",EDGE,"E7")])],"isStart":false});
            var Q3;
            Q3=makeQuery(id+"F4.opExtrude","CAP_EDGE",EDGE,{"disambiguationData":[OSD([sQuery(id+"F3.wireOp",EDGE,"E7")])],"isStart":true});
            fillet(context, id + "F32", {"entities" : qUnion([Q0, Q1, Q2, Q3]), "radius" : 5 * mm, "tangentPropagation" : true, "allowEdgeOverflow" : false});
        }
        {
            var Q0;
            {var subQ0=sQuery(id+"F6.wireOp",EDGE,"E12.0");var subQ1=sQuery(id+"F6.wireOp",EDGE,"E11");var subQ2=sQuery(id+"F6.wireOp",EDGE,"E10");var subQ3=sQuery(id+"F6.wireOp",EDGE,"E9");Q0=makeQuery(id+"F8.boolean.opBoolean","SPLIT",EDGE,{"disambiguationData":[TD([makeQuery(id+"F8.opExtrude","CAP_FACE",FACE,{"disambiguationData":[OSD([subQ3,subQ2,subQ1,subQ0])],"isStart":false})])],"derivedFrom":makeQuery(id+"F8.opExtrude","SWEPT_EDGE",EDGE,{"disambiguationData":[OSD([subQ2,subQ0])]})});}
            var Q1;
            {var subQ0=sQuery(id+"F6.wireOp",EDGE,"E12.0");var subQ1=sQuery(id+"F6.wireOp",EDGE,"E11");var subQ2=sQuery(id+"F6.wireOp",EDGE,"E10");var subQ3=sQuery(id+"F6.wireOp",EDGE,"E9");Q1=makeQuery(id+"F8.boolean.opBoolean","SPLIT",EDGE,{"disambiguationData":[TD([makeQuery(id+"F8.opExtrude","CAP_FACE",FACE,{"disambiguationData":[OSD([subQ3,subQ2,subQ1,subQ0])],"isStart":true})])],"derivedFrom":makeQuery(id+"F8.opExtrude","SWEPT_EDGE",EDGE,{"disambiguationData":[OSD([subQ2,subQ0])]})});}
            var Q2;
            Q2=makeQuery(id+"F10.boolean.opBoolean","COPY",EDGE,{"derivedFrom":makeQuery(id+"F10.opExtrude","SWEPT_EDGE",EDGE,{"disambiguationData":[OSD([sQuery(id+"F9.wireOp",EDGE,"E17.0"),sQuery(id+"F9.wireOp",EDGE,"E17.1")])]})});
            var Q3;
            Q3=makeQuery(id+"F10.boolean.opBoolean","COPY",EDGE,{"derivedFrom":makeQuery(id+"F10.opExtrude","SWEPT_EDGE",EDGE,{"disambiguationData":[OSD([sQuery(id+"F9.wireOp",EDGE,"E17.0"),sQuery(id+"F9.wireOp",EDGE,"E17.3")])]})});
            var Q4;
            {var subQ0=sQuery(id+"F6.wireOp",EDGE,"E12.0");var subQ1=sQuery(id+"F6.wireOp",EDGE,"E11");var subQ2=sQuery(id+"F6.wireOp",EDGE,"E10");var subQ3=sQuery(id+"F6.wireOp",EDGE,"E9");Q4=makeQuery(id+"F8.boolean.opBoolean","SPLIT",EDGE,{"disambiguationData":[TD([makeQuery(id+"F8.opExtrude","CAP_FACE",FACE,{"disambiguationData":[OSD([subQ3,subQ2,subQ1,subQ0])],"isStart":true})])],"derivedFrom":makeQuery(id+"F8.opExtrude","SWEPT_EDGE",EDGE,{"disambiguationData":[OSD([subQ1,subQ0])]})});}
            var Q5;
            {var subQ0=sQuery(id+"F6.wireOp",EDGE,"E12.0");var subQ1=sQuery(id+"F6.wireOp",EDGE,"E11");var subQ2=sQuery(id+"F6.wireOp",EDGE,"E10");var subQ3=sQuery(id+"F6.wireOp",EDGE,"E9");Q5=makeQuery(id+"F8.boolean.opBoolean","SPLIT",EDGE,{"disambiguationData":[TD([makeQuery(id+"F8.opExtrude","CAP_FACE",FACE,{"disambiguationData":[OSD([subQ3,subQ2,subQ1,subQ0])],"isStart":false})])],"derivedFrom":makeQuery(id+"F8.opExtrude","SWEPT_EDGE",EDGE,{"disambiguationData":[OSD([subQ1,subQ0])]})});}
            var Q6;
            Q6=makeQuery(id+"FxfVUJS9z9ZERBC_3.1.F10.boolean.opBoolean","COPY",EDGE,{"derivedFrom":makeQuery(id+"FxfVUJS9z9ZERBC_3.1.F10.opExtrude","SWEPT_EDGE",EDGE,{"disambiguationData":[OSD([sQuery(id+"F9.wireOp",EDGE,"E17.0"),sQuery(id+"F9.wireOp",EDGE,"E17.3")])]})});
            var Q7;
            Q7=makeQuery(id+"FxfVUJS9z9ZERBC_3.1.F10.boolean.opBoolean","COPY",EDGE,{"derivedFrom":makeQuery(id+"FxfVUJS9z9ZERBC_3.1.F10.opExtrude","SWEPT_EDGE",EDGE,{"disambiguationData":[OSD([sQuery(id+"F9.wireOp",EDGE,"E17.0"),sQuery(id+"F9.wireOp",EDGE,"E17.1")])]})});
            var Q8;
            Q8=makeQuery(id+"FxfVUJS9z9ZERBC_3.1.F10.boolean.opBoolean","COPY",EDGE,{"derivedFrom":makeQuery(id+"FxfVUJS9z9ZERBC_3.1.F10.opExtrude","SWEPT_EDGE",EDGE,{"disambiguationData":[OSD([sQuery(id+"F9.wireOp",EDGE,"E17.1"),sQuery(id+"F9.wireOp",EDGE,"E17.2")])]})});
            var Q9;
            Q9=makeQuery(id+"FxfVUJS9z9ZERBC_3.1.F10.boolean.opBoolean","COPY",EDGE,{"derivedFrom":makeQuery(id+"FxfVUJS9z9ZERBC_3.1.F10.opExtrude","SWEPT_EDGE",EDGE,{"disambiguationData":[OSD([sQuery(id+"F9.wireOp",EDGE,"E17.2"),sQuery(id+"F9.wireOp",EDGE,"E17.3")])]})});
            var Q10;
            {var subQ0=sQuery(id+"F12.wireOp",EDGE,"E22.0");var subQ1=sQuery(id+"F12.wireOp",EDGE,"E21");var subQ2=sQuery(id+"F12.wireOp",EDGE,"E20");var subQ3=sQuery(id+"F12.wireOp",EDGE,"E19");Q10=makeQuery(id+"F14.boolean.opBoolean","SPLIT",EDGE,{"disambiguationData":[TD([makeQuery(id+"F13.opExtrude","CAP_FACE",FACE,{"disambiguationData":[OSD([sQuery(id+"F12.wireOp",EDGE,"E18"),subQ3,subQ2,subQ1])],"isStart":true})])],"derivedFrom":makeQuery(id+"F14.opExtrude","SWEPT_EDGE",EDGE,{"disambiguationData":[OSD([subQ1,subQ0])]})});}
            var Q11;
            {var subQ0=sQuery(id+"F12.wireOp",EDGE,"E22.0");var subQ1=sQuery(id+"F12.wireOp",EDGE,"E21");var subQ2=sQuery(id+"F12.wireOp",EDGE,"E20");var subQ3=sQuery(id+"F12.wireOp",EDGE,"E19");Q11=makeQuery(id+"F14.boolean.opBoolean","SPLIT",EDGE,{"disambiguationData":[TD([makeQuery(id+"F13.opExtrude","CAP_FACE",FACE,{"disambiguationData":[OSD([sQuery(id+"F12.wireOp",EDGE,"E18"),subQ3,subQ2,subQ1])],"isStart":false})])],"derivedFrom":makeQuery(id+"F14.opExtrude","SWEPT_EDGE",EDGE,{"disambiguationData":[OSD([subQ1,subQ0])]})});}
            var Q12;
            {var subQ0=sQuery(id+"F12.wireOp",EDGE,"E22.0");var subQ1=sQuery(id+"F12.wireOp",EDGE,"E21");var subQ2=sQuery(id+"F12.wireOp",EDGE,"E20");var subQ3=sQuery(id+"F12.wireOp",EDGE,"E19");Q12=makeQuery(id+"F14.boolean.opBoolean","SPLIT",EDGE,{"disambiguationData":[TD([makeQuery(id+"F13.opExtrude","CAP_FACE",FACE,{"disambiguationData":[OSD([sQuery(id+"F12.wireOp",EDGE,"E18"),subQ3,subQ2,subQ1])],"isStart":true})])],"derivedFrom":makeQuery(id+"F14.opExtrude","SWEPT_EDGE",EDGE,{"disambiguationData":[OSD([subQ2,subQ0])]})});}
            var Q13;
            {var subQ0=sQuery(id+"F12.wireOp",EDGE,"E22.0");var subQ1=sQuery(id+"F12.wireOp",EDGE,"E21");var subQ2=sQuery(id+"F12.wireOp",EDGE,"E20");var subQ3=sQuery(id+"F12.wireOp",EDGE,"E19");Q13=makeQuery(id+"F14.boolean.opBoolean","SPLIT",EDGE,{"disambiguationData":[TD([makeQuery(id+"F13.opExtrude","CAP_FACE",FACE,{"disambiguationData":[OSD([sQuery(id+"F12.wireOp",EDGE,"E18"),subQ3,subQ2,subQ1])],"isStart":false})])],"derivedFrom":makeQuery(id+"F14.opExtrude","SWEPT_EDGE",EDGE,{"disambiguationData":[OSD([subQ2,subQ0])]})});}
            var Q14;
            Q14=makeQuery(id+"FPmtPOSjaGEUDap_4.1.F16.boolean.opBoolean","COPY",EDGE,{"derivedFrom":makeQuery(id+"FPmtPOSjaGEUDap_4.1.F16.opExtrude","SWEPT_EDGE",EDGE,{"disambiguationData":[OSD([sQuery(id+"F15.wireOp",EDGE,"E23.0"),sQuery(id+"F15.wireOp",EDGE,"E23.3")])]})});
            var Q15;
            Q15=makeQuery(id+"FPmtPOSjaGEUDap_4.1.F16.boolean.opBoolean","COPY",EDGE,{"derivedFrom":makeQuery(id+"FPmtPOSjaGEUDap_4.1.F16.opExtrude","SWEPT_EDGE",EDGE,{"disambiguationData":[OSD([sQuery(id+"F15.wireOp",EDGE,"E23.0"),sQuery(id+"F15.wireOp",EDGE,"E23.1")])]})});
            var Q16;
            Q16=makeQuery(id+"FPmtPOSjaGEUDap_4.1.F16.boolean.opBoolean","COPY",EDGE,{"derivedFrom":makeQuery(id+"FPmtPOSjaGEUDap_4.1.F16.opExtrude","SWEPT_EDGE",EDGE,{"disambiguationData":[OSD([sQuery(id+"F15.wireOp",EDGE,"E23.1"),sQuery(id+"F15.wireOp",EDGE,"E23.2")])]})});
            var Q17;
            Q17=makeQuery(id+"FPmtPOSjaGEUDap_4.1.F16.boolean.opBoolean","COPY",EDGE,{"derivedFrom":makeQuery(id+"FPmtPOSjaGEUDap_4.1.F16.opExtrude","SWEPT_EDGE",EDGE,{"disambiguationData":[OSD([sQuery(id+"F15.wireOp",EDGE,"E23.2"),sQuery(id+"F15.wireOp",EDGE,"E23.3")])]})});
            var Q18;
            Q18=makeQuery(id+"FINGwCLTqzDAgHr_5.1.F22.boolean.opBoolean","COPY",EDGE,{"derivedFrom":makeQuery(id+"FINGwCLTqzDAgHr_5.1.F22.opExtrude","SWEPT_EDGE",EDGE,{"disambiguationData":[OSD([sQuery(id+"F21.wireOp",EDGE,"E29.2"),sQuery(id+"F21.wireOp",EDGE,"E29.3")])]})});
            var Q19;
            Q19=makeQuery(id+"FINGwCLTqzDAgHr_5.1.F22.boolean.opBoolean","COPY",EDGE,{"derivedFrom":makeQuery(id+"FINGwCLTqzDAgHr_5.1.F22.opExtrude","SWEPT_EDGE",EDGE,{"disambiguationData":[OSD([sQuery(id+"F21.wireOp",EDGE,"E29.1"),sQuery(id+"F21.wireOp",EDGE,"E29.2")])]})});
            var Q20;
            Q20=makeQuery(id+"FINGwCLTqzDAgHr_5.1.F22.boolean.opBoolean","COPY",EDGE,{"derivedFrom":makeQuery(id+"FINGwCLTqzDAgHr_5.1.F22.opExtrude","SWEPT_EDGE",EDGE,{"disambiguationData":[OSD([sQuery(id+"F21.wireOp",EDGE,"E29.0"),sQuery(id+"F21.wireOp",EDGE,"E29.1")])]})});
            var Q21;
            Q21=makeQuery(id+"FINGwCLTqzDAgHr_5.1.F22.boolean.opBoolean","COPY",EDGE,{"derivedFrom":makeQuery(id+"FINGwCLTqzDAgHr_5.1.F22.opExtrude","SWEPT_EDGE",EDGE,{"disambiguationData":[OSD([sQuery(id+"F21.wireOp",EDGE,"E29.0"),sQuery(id+"F21.wireOp",EDGE,"E29.3")])]})});
            var Q22;
            {var subQ0=sQuery(id+"F18.wireOp",EDGE,"E28.0");var subQ1=sQuery(id+"F18.wireOp",EDGE,"E27");var subQ2=sQuery(id+"F18.wireOp",EDGE,"E26");var subQ3=sQuery(id+"F18.wireOp",EDGE,"E25");Q22=makeQuery(id+"F20.boolean.opBoolean","SPLIT",EDGE,{"disambiguationData":[TD([makeQuery(id+"F19.opExtrude","CAP_FACE",FACE,{"disambiguationData":[OSD([sQuery(id+"F18.wireOp",EDGE,"E24"),subQ3,subQ2,subQ1])],"isStart":true})])],"derivedFrom":makeQuery(id+"F20.opExtrude","SWEPT_EDGE",EDGE,{"disambiguationData":[OSD([subQ2,subQ0])]})});}
            var Q23;
            {var subQ0=sQuery(id+"F18.wireOp",EDGE,"E28.0");var subQ1=sQuery(id+"F18.wireOp",EDGE,"E27");var subQ2=sQuery(id+"F18.wireOp",EDGE,"E26");var subQ3=sQuery(id+"F18.wireOp",EDGE,"E25");Q23=makeQuery(id+"F20.boolean.opBoolean","SPLIT",EDGE,{"disambiguationData":[TD([makeQuery(id+"F19.opExtrude","CAP_FACE",FACE,{"disambiguationData":[OSD([sQuery(id+"F18.wireOp",EDGE,"E24"),subQ3,subQ2,subQ1])],"isStart":false})])],"derivedFrom":makeQuery(id+"F20.opExtrude","SWEPT_EDGE",EDGE,{"disambiguationData":[OSD([subQ2,subQ0])]})});}
            var Q24;
            {var subQ0=sQuery(id+"F18.wireOp",EDGE,"E28.0");var subQ1=sQuery(id+"F18.wireOp",EDGE,"E27");var subQ2=sQuery(id+"F18.wireOp",EDGE,"E26");var subQ3=sQuery(id+"F18.wireOp",EDGE,"E25");Q24=makeQuery(id+"F20.boolean.opBoolean","SPLIT",EDGE,{"disambiguationData":[TD([makeQuery(id+"F19.opExtrude","CAP_FACE",FACE,{"disambiguationData":[OSD([sQuery(id+"F18.wireOp",EDGE,"E24"),subQ3,subQ2,subQ1])],"isStart":true})])],"derivedFrom":makeQuery(id+"F20.opExtrude","SWEPT_EDGE",EDGE,{"disambiguationData":[OSD([subQ1,subQ0])]})});}
            var Q25;
            {var subQ0=sQuery(id+"F18.wireOp",EDGE,"E28.0");var subQ1=sQuery(id+"F18.wireOp",EDGE,"E27");var subQ2=sQuery(id+"F18.wireOp",EDGE,"E26");var subQ3=sQuery(id+"F18.wireOp",EDGE,"E25");Q25=makeQuery(id+"F20.boolean.opBoolean","SPLIT",EDGE,{"disambiguationData":[TD([makeQuery(id+"F19.opExtrude","CAP_FACE",FACE,{"disambiguationData":[OSD([sQuery(id+"F18.wireOp",EDGE,"E24"),subQ3,subQ2,subQ1])],"isStart":false})])],"derivedFrom":makeQuery(id+"F20.opExtrude","SWEPT_EDGE",EDGE,{"disambiguationData":[OSD([subQ1,subQ0])]})});}
            fillet(context, id + "F33", {"entities" : qUnion([Q0, Q1, Q2, Q3, Q4, Q5, Q6, Q7, Q8, Q9, Q10, Q11, Q12, Q13, Q14, Q15, Q16, Q17, Q18, Q19, Q20, Q21, Q22, Q23, Q24, Q25]), "radius" : 2 * mm, "tangentPropagation" : true, "allowEdgeOverflow" : false});
        }
        {
            var Q0;
            Q0=makeQuery(id+"F29.boolean.opBoolean","INTERSECT",EDGE,{"derivedFrom":[makeQuery(id+"F24.opRevolve","SWEPT_FACE",FACE,{"disambiguationData":[OSD([sQuery(id+"F23.wireOp",EDGE,"E62.right")])]}),makeQuery(id+"F29.opExtrude","SWEPT_FACE",FACE,{"disambiguationData":[OSD([sQuery(id+"F28.wireOp",EDGE,"E84.left")])]})]});
            var Q1;
            Q1=makeQuery(id+"F29.boolean.opBoolean","INTERSECT",EDGE,{"derivedFrom":[makeQuery(id+"F24.opRevolve","SWEPT_FACE",FACE,{"disambiguationData":[OSD([sQuery(id+"F23.wireOp",EDGE,"E62.right")])]}),makeQuery(id+"F29.opExtrude","SWEPT_FACE",FACE,{"disambiguationData":[OSD([sQuery(id+"F28.wireOp",EDGE,"E84.top")])]})]});
            var Q2;
            Q2=makeQuery(id+"F29.boolean.opBoolean","INTERSECT",EDGE,{"derivedFrom":[makeQuery(id+"F24.opRevolve","SWEPT_FACE",FACE,{"disambiguationData":[OSD([sQuery(id+"F23.wireOp",EDGE,"E62.right")])]}),makeQuery(id+"F29.opExtrude","SWEPT_FACE",FACE,{"disambiguationData":[OSD([sQuery(id+"F28.wireOp",EDGE,"E84.right")])]})]});
            var Q3;
            Q3=makeQuery(id+"F29.boolean.opBoolean","INTERSECT",EDGE,{"derivedFrom":[makeQuery(id+"F24.opRevolve","SWEPT_FACE",FACE,{"disambiguationData":[OSD([sQuery(id+"F23.wireOp",EDGE,"E62.right")])]}),makeQuery(id+"F29.opExtrude","SWEPT_FACE",FACE,{"disambiguationData":[OSD([sQuery(id+"F28.wireOp",EDGE,"E84.bottom")])]})]});
            var Q4;
            Q4=makeQuery(id+"F29.boolean.opBoolean","INTERSECT",EDGE,{"derivedFrom":[makeQuery(id+"F25.opRevolve","SWEPT_FACE",FACE,{"disambiguationData":[OSD([sQuery(id+"F23.wireOp",EDGE,"E67")])]}),makeQuery(id+"F29.opExtrude","SWEPT_FACE",FACE,{"disambiguationData":[OSD([sQuery(id+"F28.wireOp",EDGE,"E89.top")])]})]});
            var Q5;
            Q5=makeQuery(id+"F29.boolean.opBoolean","INTERSECT",EDGE,{"derivedFrom":[makeQuery(id+"F25.opRevolve","SWEPT_FACE",FACE,{"disambiguationData":[OSD([sQuery(id+"F23.wireOp",EDGE,"E67")])]}),makeQuery(id+"F29.opExtrude","SWEPT_FACE",FACE,{"disambiguationData":[OSD([sQuery(id+"F28.wireOp",EDGE,"E89.right")])]})]});
            var Q6;
            Q6=makeQuery(id+"F29.boolean.opBoolean","INTERSECT",EDGE,{"derivedFrom":[makeQuery(id+"F25.opRevolve","SWEPT_FACE",FACE,{"disambiguationData":[OSD([sQuery(id+"F23.wireOp",EDGE,"E67")])]}),makeQuery(id+"F29.opExtrude","SWEPT_FACE",FACE,{"disambiguationData":[OSD([sQuery(id+"F28.wireOp",EDGE,"E89.left")])]})]});
            var Q7;
            Q7=makeQuery(id+"F29.boolean.opBoolean","INTERSECT",EDGE,{"derivedFrom":[makeQuery(id+"F25.opRevolve","SWEPT_FACE",FACE,{"disambiguationData":[OSD([sQuery(id+"F23.wireOp",EDGE,"E67")])]}),makeQuery(id+"F29.opExtrude","SWEPT_FACE",FACE,{"disambiguationData":[OSD([sQuery(id+"F28.wireOp",EDGE,"E89.bottom")])]})]});
            var Q8;
            Q8=makeQuery(id+"F29.boolean.opBoolean","INTERSECT",EDGE,{"derivedFrom":[makeQuery(id+"F26.opRevolve","SWEPT_FACE",FACE,{"disambiguationData":[OSD([sQuery(id+"F23.wireOp",EDGE,"E73")])]}),makeQuery(id+"F29.opExtrude","SWEPT_FACE",FACE,{"disambiguationData":[OSD([sQuery(id+"F28.wireOp",EDGE,"E92.top")])]})]});
            var Q9;
            Q9=makeQuery(id+"F29.boolean.opBoolean","INTERSECT",EDGE,{"derivedFrom":[makeQuery(id+"F26.opRevolve","SWEPT_FACE",FACE,{"disambiguationData":[OSD([sQuery(id+"F23.wireOp",EDGE,"E73")])]}),makeQuery(id+"F29.opExtrude","SWEPT_FACE",FACE,{"disambiguationData":[OSD([sQuery(id+"F28.wireOp",EDGE,"E92.right")])]})]});
            var Q10;
            Q10=makeQuery(id+"F29.boolean.opBoolean","INTERSECT",EDGE,{"derivedFrom":[makeQuery(id+"F26.opRevolve","SWEPT_FACE",FACE,{"disambiguationData":[OSD([sQuery(id+"F23.wireOp",EDGE,"E73")])]}),makeQuery(id+"F29.opExtrude","SWEPT_FACE",FACE,{"disambiguationData":[OSD([sQuery(id+"F28.wireOp",EDGE,"E92.bottom")])]})]});
            var Q11;
            Q11=makeQuery(id+"F29.boolean.opBoolean","INTERSECT",EDGE,{"derivedFrom":[makeQuery(id+"F26.opRevolve","SWEPT_FACE",FACE,{"disambiguationData":[OSD([sQuery(id+"F23.wireOp",EDGE,"E73")])]}),makeQuery(id+"F29.opExtrude","SWEPT_FACE",FACE,{"disambiguationData":[OSD([sQuery(id+"F28.wireOp",EDGE,"E92.left")])]})]});
            var Q12;
            Q12=makeQuery(id+"F29.boolean.opBoolean","INTERSECT",EDGE,{"derivedFrom":[makeQuery(id+"F27.opRevolve","SWEPT_FACE",FACE,{"disambiguationData":[OSD([sQuery(id+"F23.wireOp",EDGE,"E79")])]}),makeQuery(id+"F29.opExtrude","SWEPT_FACE",FACE,{"disambiguationData":[OSD([sQuery(id+"F28.wireOp",EDGE,"E95.top")])]})]});
            var Q13;
            Q13=makeQuery(id+"F29.boolean.opBoolean","INTERSECT",EDGE,{"derivedFrom":[makeQuery(id+"F27.opRevolve","SWEPT_FACE",FACE,{"disambiguationData":[OSD([sQuery(id+"F23.wireOp",EDGE,"E79")])]}),makeQuery(id+"F29.opExtrude","SWEPT_FACE",FACE,{"disambiguationData":[OSD([sQuery(id+"F28.wireOp",EDGE,"E95.right")])]})]});
            var Q14;
            Q14=makeQuery(id+"F29.boolean.opBoolean","INTERSECT",EDGE,{"derivedFrom":[makeQuery(id+"F27.opRevolve","SWEPT_FACE",FACE,{"disambiguationData":[OSD([sQuery(id+"F23.wireOp",EDGE,"E79")])]}),makeQuery(id+"F29.opExtrude","SWEPT_FACE",FACE,{"disambiguationData":[OSD([sQuery(id+"F28.wireOp",EDGE,"E95.bottom")])]})]});
            var Q15;
            Q15=makeQuery(id+"F29.boolean.opBoolean","INTERSECT",EDGE,{"derivedFrom":[makeQuery(id+"F27.opRevolve","SWEPT_FACE",FACE,{"disambiguationData":[OSD([sQuery(id+"F23.wireOp",EDGE,"E79")])]}),makeQuery(id+"F29.opExtrude","SWEPT_FACE",FACE,{"disambiguationData":[OSD([sQuery(id+"F28.wireOp",EDGE,"E95.left")])]})]});
            chamfer(context, id + "F34", {"entities" : qUnion([Q0, Q1, Q2, Q3, Q4, Q5, Q6, Q7, Q8, Q9, Q10, Q11, Q12, Q13, Q14, Q15]), "width" : 3.4 * mm, "tangentPropagation" : true});
        }
    });
